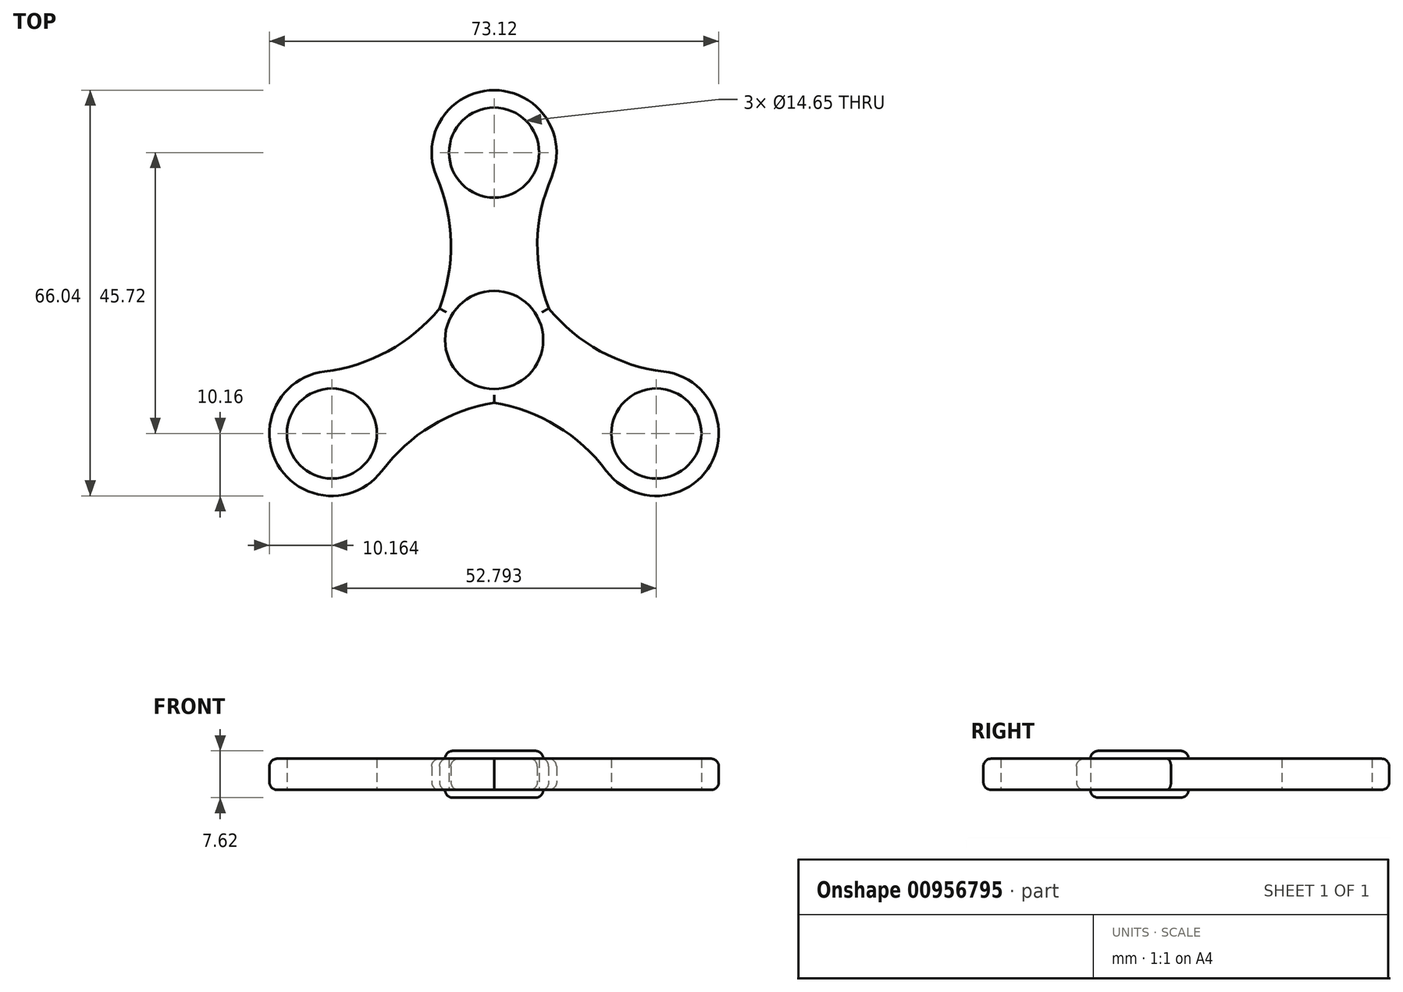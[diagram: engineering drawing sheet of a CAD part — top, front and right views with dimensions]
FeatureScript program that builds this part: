
annotation { "Feature Type Name" : "Feature", "Feature Type Description" : "" }
export const myFeature = defineFeature(function(context is Context, id is Id, definition is map)
    precondition{}
    {
        {
            var Q0;
            Q0=qCreatedBy(makeId("Top.planeOp"),FACE);
            var sketch = newSketch(context, id + "F0", { "sketchPlane" : qUnion([Q0])});
            skArc(sketch, "E0", {"start": v(9.34, 26.48) * mm, "mid": v(0, 40.64) * mm, "end": v(-9.34, 26.48) * mm});
            skPoint(sketch, "E1.start.orphan", {"position": v(-10.16, 0) * mm});
            skPoint(sketch, "E2.orphan", {"position": v(-15.24, 0) * mm});
            skArc(sketch, "E3", {"start": v(-8.88, 5.13) * mm, "mid": v(-7.04, 15.85) * mm, "end": v(-9.34, 26.48) * mm});
            skPoint(sketch, "E4.start.orphan", {"position": v(-35.56, 0) * mm});
            skPoint(sketch, "E5.start.orphan", {"position": v(43.18, 0) * mm});
            skArc(sketch, "E6", {"start": v(9.34, 26.48) * mm, "mid": v(7.04, 15.85) * mm, "end": v(8.88, 5.13) * mm});
            skPoint(sketch, "E7.orphan", {"position": v(35.56, 0) * mm});
            skPoint(sketch, "E8.orphan", {"position": v(10.97, 0) * mm});
            skPoint(sketch, "E9.start.orphan", {"position": v(0, 15.24) * mm});
            skCircle(sketch, "E10", {"center": v(0, 30.48) * mm, "radius": 7.32 * mm});
            skArc(sketch, "E11.1.0", {"start": v(-27.6, -5.15) * mm, "mid": v(-17.24, -1.83) * mm, "end": v(-8.88, 5.13) * mm});
            skArc(sketch, "E11.1.1", {"start": v(-27.6, -5.15) * mm, "mid": v(-35.2, -20.32) * mm, "end": v(-18.26, -21.33) * mm});
            skCircle(sketch, "E11.1.2", {"center": v(-26.4, -15.24) * mm, "radius": 7.32 * mm});
            skArc(sketch, "E11.1.3", {"start": v(0, -10.26) * mm, "mid": v(-10.2, -14.02) * mm, "end": v(-18.26, -21.33) * mm});
            skArc(sketch, "E11.2.0", {"start": v(18.26, -21.33) * mm, "mid": v(10.2, -14.02) * mm, "end": v(0, -10.26) * mm});
            skArc(sketch, "E11.2.1", {"start": v(18.26, -21.33) * mm, "mid": v(35.2, -20.32) * mm, "end": v(27.6, -5.15) * mm});
            skCircle(sketch, "E11.2.2", {"center": v(26.4, -15.24) * mm, "radius": 7.32 * mm});
            skArc(sketch, "E11.2.3", {"start": v(8.88, 5.13) * mm, "mid": v(17.24, -1.83) * mm, "end": v(27.6, -5.15) * mm});
            skPoint(sketch, "E11.center", {"position": v(0, 0) * mm});
            skPoint(sketch, "E12.orphan", {"position": v(8.14, 6.09) * mm});
            skPoint(sketch, "E13.orphan", {"position": v(9.34, 4) * mm});
            skPoint(sketch, "E14.orphan", {"position": v(1.2, -10.09) * mm});
            skPoint(sketch, "E15.orphan", {"position": v(-1.2, -10.09) * mm});
            skPoint(sketch, "E16.orphan", {"position": v(-9.34, 4) * mm});
            skPoint(sketch, "E17.orphan", {"position": v(-8.14, 6.09) * mm});
            skCircle(sketch, "E18", {"center": v(0, 0) * mm, "radius": 7.98 * mm});
            skSolve(sketch);
        }
        {
            var Q0;
            Q0=makeQuery(id+"F0.imprint","IMPRINT",FACE,{"disambiguationData":[TD([[makeQuery(id+"F0.imprint","IMPRINT",EDGE,{"derivedFrom":sQuery(id+"F0.wireOp",EDGE,"E0")}),1.0]])]});
            var Q1;
            Q1=makeQuery(id+"F0.imprint","IMPRINT",FACE,{"disambiguationData":[TD([[makeQuery(id+"F0.imprint","IMPRINT",EDGE,{"derivedFrom":sQuery(id+"F0.wireOp",EDGE,"E18")}),1.0]])]});
            extrude(context, id + "F1", {"entities" : qUnion([Q0, Q1]), "depth" : 5.08 * mm, "offsetDistance" : 25.4 * mm});
        }
        {
            var Q0;
            Q0=makeQuery(id+"F0.imprint","IMPRINT",FACE,{"disambiguationData":[TD([[makeQuery(id+"F0.imprint","IMPRINT",EDGE,{"derivedFrom":sQuery(id+"F0.wireOp",EDGE,"E18")}),1.0]])]});
            extrude(context, id + "F2", {"entities" : qUnion([Q0]), "operationType" : NewBodyOperationType.ADD, "depth" : 6.35 * mm, "offsetDistance" : 25.4 * mm});
        }
        {
            var Q0;
            Q0=makeQuery(id+"F0.imprint","IMPRINT",FACE,{"disambiguationData":[TD([[makeQuery(id+"F0.imprint","IMPRINT",EDGE,{"derivedFrom":sQuery(id+"F0.wireOp",EDGE,"E18")}),1.0]])]});
            extrude(context, id + "F3", {"entities" : qUnion([Q0]), "operationType" : NewBodyOperationType.ADD, "oppositeDirection" : true, "depth" : 1.27 * mm, "offsetDistance" : 25.4 * mm});
        }
        {
            var Q0;
            Q0=makeQuery(id+"F1.opExtrude","CAP_EDGE",EDGE,{"disambiguationData":[OSD([sQuery(id+"F0.wireOp",EDGE,"E11.2.0")])],"isStart":false});
            var Q1;
            Q1=makeQuery(id+"F1.opExtrude","CAP_EDGE",EDGE,{"disambiguationData":[OSD([sQuery(id+"F0.wireOp",EDGE,"E11.1.3")])],"isStart":false});
            var Q2;
            Q2=makeQuery(id+"F1.opExtrude","CAP_EDGE",EDGE,{"disambiguationData":[OSD([sQuery(id+"F0.wireOp",EDGE,"E11.2.0")])],"isStart":true});
            var Q3;
            Q3=makeQuery(id+"F1.opExtrude","CAP_EDGE",EDGE,{"disambiguationData":[OSD([sQuery(id+"F0.wireOp",EDGE,"E11.1.3")])],"isStart":true});
            var Q4;
            Q4=makeQuery(id+"F1.opExtrude","CAP_EDGE",EDGE,{"disambiguationData":[OSD([sQuery(id+"F0.wireOp",EDGE,"E3")])],"isStart":false});
            var Q5;
            Q5=makeQuery(id+"F1.opExtrude","CAP_EDGE",EDGE,{"disambiguationData":[OSD([sQuery(id+"F0.wireOp",EDGE,"E3")])],"isStart":true});
            var Q6;
            Q6=makeQuery(id+"F3.opExtrude","CAP_EDGE",EDGE,{"disambiguationData":[OSD([sQuery(id+"F0.wireOp",EDGE,"E18")])],"isStart":false});
            var Q7;
            Q7=makeQuery(id+"F2.opExtrude","CAP_EDGE",EDGE,{"disambiguationData":[OSD([sQuery(id+"F0.wireOp",EDGE,"E18")])],"isStart":false});
            fillet(context, id + "F4", {"entities" : qUnion([Q0, Q1, Q2, Q3, Q4, Q5, Q6, Q7]), "radius" : 1.27 * mm, "tangentPropagation" : true, "allowEdgeOverflow" : false});
        }
    });
